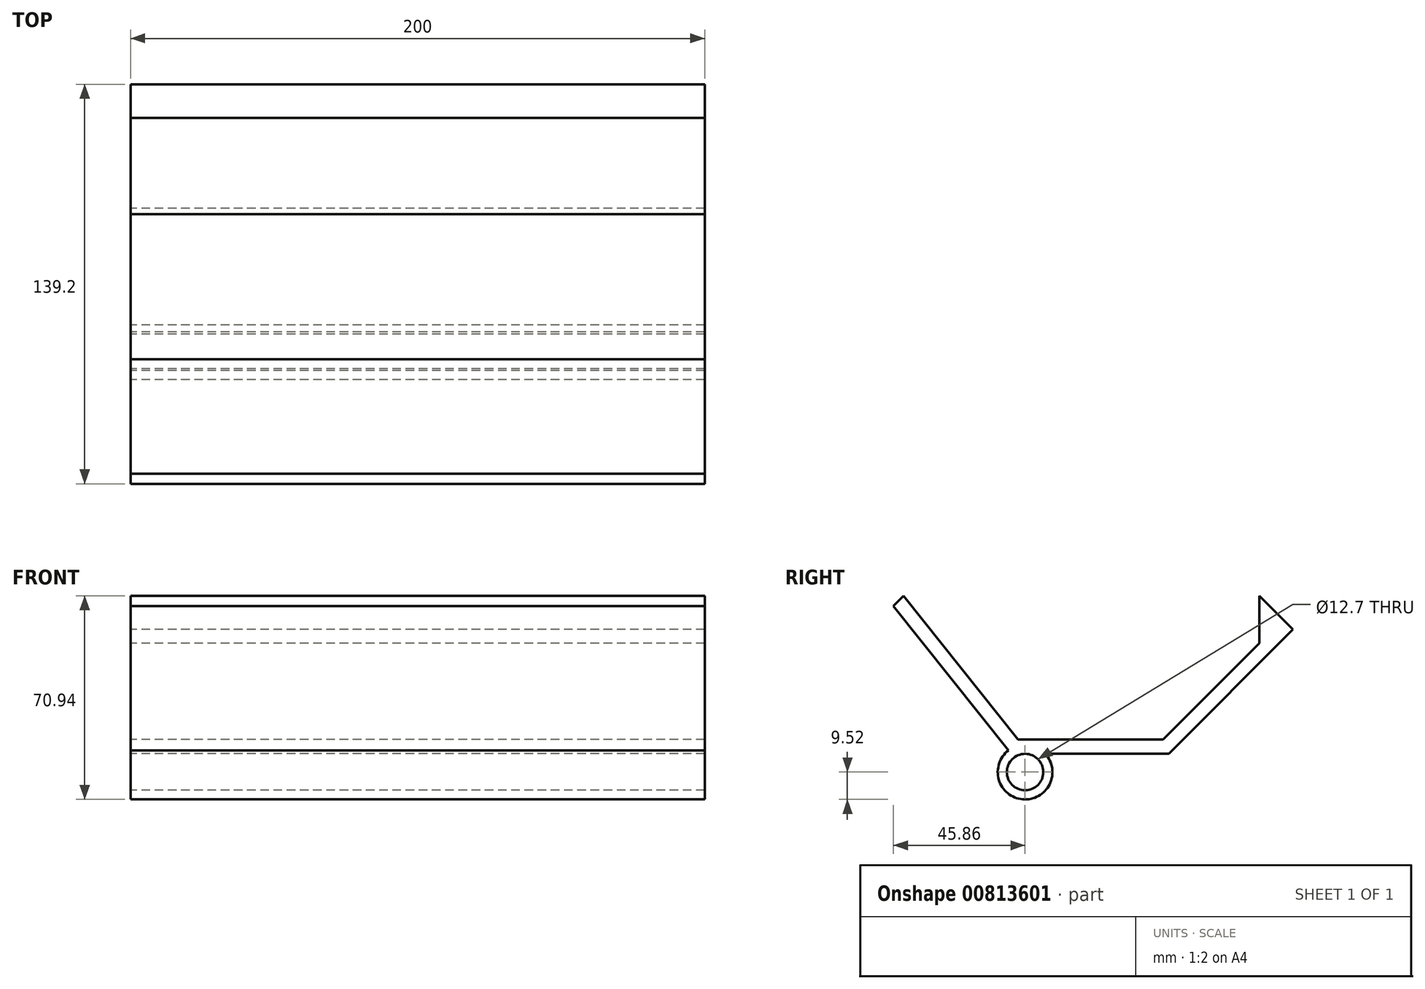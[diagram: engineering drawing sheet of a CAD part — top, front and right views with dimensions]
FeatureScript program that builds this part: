
annotation { "Feature Type Name" : "Feature", "Feature Type Description" : "" }
export const myFeature = defineFeature(function(context is Context, id is Id, definition is map)
    precondition{}
    {
        {
            var Q0;
            Q0=qCreatedBy(makeId("Right.planeOp"),FACE);
            var sketch = newSketch(context, id + "F0", { "sketchPlane" : qUnion([Q0])});
            skCircle(sketch, "E0", {"center": v(0, 0) * mm, "radius": 6.35 * mm});
            skCircle(sketch, "E1", {"center": v(0, 0) * mm, "radius": 9.53 * mm});
            skLineSegment(sketch, "E2.0", {"start": v(50.1, 6.42) * mm, "end": v(-4.86, 6.42) * mm});
            skLineSegment(sketch, "E2.1", {"start": v(-4.86, 6.42) * mm, "end": v(-45.86, 57.86) * mm});
            skLineSegment(sketch, "E2.7", {"start": v(93.34, 49.66) * mm, "end": v(50.1, 6.42) * mm});
            skPoint(sketch, "E2.0.midPoint", {"position": v(22.62, 6.42) * mm});
            skLineSegment(sketch, "E3.0", {"start": v(-2.45, 11.42) * mm, "end": v(-42.3, 61.42) * mm});
            skLineSegment(sketch, "E3.1", {"start": v(48.03, 11.42) * mm, "end": v(-2.45, 11.42) * mm});
            skLineSegment(sketch, "E4", {"start": v(-42.3, 61.42) * mm, "end": v(-45.86, 57.86) * mm});
            skLineSegment(sketch, "E5", {"start": v(85.43, 57.57) * mm, "end": v(93.34, 49.66) * mm});
            skLineSegment(sketch, "E6", {"start": v(81.56, 44.94) * mm, "end": v(81.56, 61.42) * mm});
            skLineSegment(sketch, "E7", {"start": v(81.56, 61.42) * mm, "end": v(85.43, 57.57) * mm});
            skLineSegment(sketch, "E8", {"start": v(81.56, 44.94) * mm, "end": v(48.03, 11.42) * mm});
            skSolve(sketch);
        }
        {
            var Q0;
            Q0 = qSketchRegion(id + "F0", true);
            extrude(context, id + "F1", {"entities" : qUnion([Q0]), "depth" : 200 * mm, "offsetDistance" : 25.4 * mm});
        }
    });
